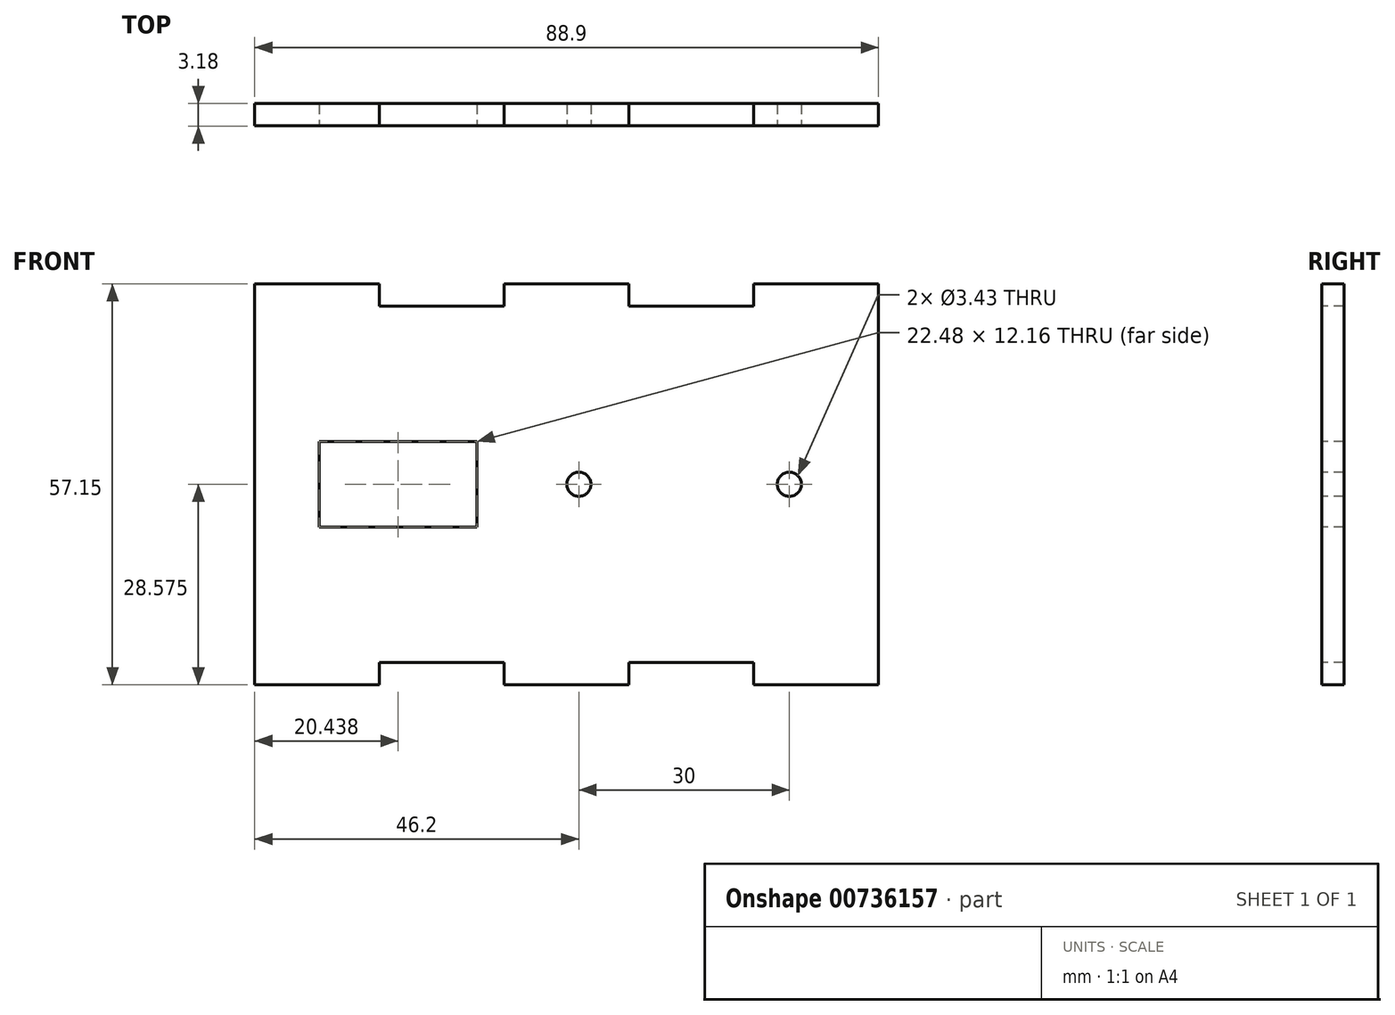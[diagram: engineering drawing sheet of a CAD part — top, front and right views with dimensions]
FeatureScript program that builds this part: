
annotation { "Feature Type Name" : "Feature", "Feature Type Description" : "" }
export const myFeature = defineFeature(function(context is Context, id is Id, definition is map)
    precondition{}
    {
        {
            var Q0;
            Q0=qCreatedBy(makeId("Top.planeOp"),FACE);
            var sketch = newSketch(context, id + "F0", { "sketchPlane" : qUnion([Q0])});
            skLineSegment(sketch, "E0.bottom", {"start": v(44.45, 9.52) * mm, "end": v(-44.45, 9.52) * mm});
            skLineSegment(sketch, "E0.top", {"start": v(44.45, -9.53) * mm, "end": v(-44.45, -9.53) * mm});
            skLineSegment(sketch, "E0.left", {"start": v(44.45, 9.52) * mm, "end": v(44.45, -9.53) * mm});
            skLineSegment(sketch, "E0.right", {"start": v(-44.45, 9.52) * mm, "end": v(-44.45, -9.53) * mm});
            skPoint(sketch, "E0.middle", {"position": v(0, 0) * mm});
            skLineSegment(sketch, "E1", {"start": v(-44.45, 6.35) * mm, "end": v(44.45, 6.35) * mm});
            skLineSegment(sketch, "E2", {"start": v(-44.45, -6.35) * mm, "end": v(44.45, -6.35) * mm});
            skSolve(sketch);
        }
        {
            var Q0;
            {var subQ0=sQuery(id+"F0.wireOp",EDGE,"E0.bottom");Q0=makeQuery(id+"F0.imprint","IMPRINT",FACE,{"disambiguationData":[TD([[makeQuery(id+"F0.imprint","IMPRINT",EDGE,{"derivedFrom":subQ0}),1.0]])]});}
            var Q1;
            {var subQ0=sQuery(id+"F0.wireOp",EDGE,"E0.top");Q1=makeQuery(id+"F0.imprint","IMPRINT",FACE,{"disambiguationData":[TD([[makeQuery(id+"F0.imprint","IMPRINT",EDGE,{"derivedFrom":subQ0}),-1.0]])]});}
            extrude(context, id + "F1", {"entities" : qUnion([Q0, Q1]), "depth" : 57.15 * mm, "offsetDistance" : 25.4 * mm});
        }
        {
            var Q0;
            Q0=makeQuery(id+"F1.opExtrude","SWEPT_FACE",FACE,{"disambiguationData":[OSD([sQuery(id+"F0.wireOp",EDGE,"E0.top")])]});
            var sketch = newSketch(context, id + "F2", { "sketchPlane" : qUnion([Q0])});
            skLineSegment(sketch, "E3", {"start": v(-44.45, 3.18) * mm, "end": v(44.45, 3.18) * mm});
            skLineSegment(sketch, "E4", {"start": v(-44.45, 53.98) * mm, "end": v(44.45, 53.98) * mm});
            skCircle(sketch, "E5", {"center": v(31.75, 28.58) * mm, "radius": 1.71 * mm});
            skPoint(sketch, "E5.centerSnap0", {"position": v(44.45, 28.58) * mm});
            skCircle(sketch, "E6", {"center": v(1.75, 28.58) * mm, "radius": 1.71 * mm});
            skLineSegment(sketch, "E7.bottom", {"start": v(-12.77, 34.66) * mm, "end": v(-35.25, 34.66) * mm});
            skLineSegment(sketch, "E7.top", {"start": v(-12.77, 22.5) * mm, "end": v(-35.25, 22.5) * mm});
            skLineSegment(sketch, "E7.left", {"start": v(-12.77, 34.66) * mm, "end": v(-12.77, 22.5) * mm});
            skLineSegment(sketch, "E7.right", {"start": v(-35.25, 34.66) * mm, "end": v(-35.25, 22.5) * mm});
            skPoint(sketch, "E7.middle", {"position": v(-24.01, 28.58) * mm});
            skLineSegment(sketch, "E8", {"start": v(-26.67, 57.15) * mm, "end": v(-26.67, 53.98) * mm});
            skLineSegment(sketch, "E9", {"start": v(-8.9, 57.15) * mm, "end": v(-8.9, 53.98) * mm});
            skLineSegment(sketch, "E10", {"start": v(8.89, 57.15) * mm, "end": v(8.89, 53.98) * mm});
            skPoint(sketch, "E10.endSnap0", {"position": v(0, 53.98) * mm});
            skLineSegment(sketch, "E11", {"start": v(26.67, 57.15) * mm, "end": v(26.67, 53.98) * mm});
            skLineSegment(sketch, "E12", {"start": v(-44.45, 28.58) * mm, "end": v(44.45, 28.58) * mm});
            skLineSegment(sketch, "E13.MirrorCS", {"start": v(26.67, 0) * mm, "end": v(26.67, 3.18) * mm});
            skLineSegment(sketch, "E14.MirrorCS", {"start": v(8.9, 0) * mm, "end": v(8.9, 3.18) * mm});
            skLineSegment(sketch, "E15.MirrorCS", {"start": v(-8.89, 0) * mm, "end": v(-8.89, 3.18) * mm});
            skLineSegment(sketch, "E16.MirrorCS", {"start": v(-26.67, 0) * mm, "end": v(-26.67, 3.18) * mm});
            skSolve(sketch);
        }
        {
            var Q0;
            {var subQ0=sQuery(id+"F2.wireOp",EDGE,"E8");Q0=makeQuery(id+"F2.imprint","IMPRINT",FACE,{"disambiguationData":[TD([[makeQuery(id+"F2.imprint","IMPRINT",EDGE,{"derivedFrom":subQ0}),1.0]])]});}
            var Q1;
            {var subQ0=sQuery(id+"F2.wireOp",EDGE,"E10");Q1=makeQuery(id+"F2.imprint","IMPRINT",FACE,{"disambiguationData":[TD([[makeQuery(id+"F2.imprint","IMPRINT",EDGE,{"derivedFrom":subQ0}),1.0]])]});}
            var Q2;
            {var subQ0=sQuery(id+"F2.wireOp",EDGE,"E15.MirrorCS");Q2=makeQuery(id+"F2.imprint","IMPRINT",FACE,{"disambiguationData":[TD([[makeQuery(id+"F2.imprint","IMPRINT",EDGE,{"derivedFrom":subQ0}),1.0]])]});}
            var Q3;
            {var subQ0=sQuery(id+"F2.wireOp",EDGE,"E13.MirrorCS");Q3=makeQuery(id+"F2.imprint","IMPRINT",FACE,{"disambiguationData":[TD([[makeQuery(id+"F2.imprint","IMPRINT",EDGE,{"derivedFrom":subQ0}),1.0]])]});}
            var Q4;
            {var subQ0=sQuery(id+"F2.wireOp",EDGE,"E7.bottom");Q4=makeQuery(id+"F2.imprint","IMPRINT",FACE,{"disambiguationData":[TD([[makeQuery(id+"F2.imprint","IMPRINT",EDGE,{"derivedFrom":subQ0}),1.0]])]});}
            var Q5;
            {var subQ0=sQuery(id+"F2.wireOp",EDGE,"E7.top");Q5=makeQuery(id+"F2.imprint","IMPRINT",FACE,{"disambiguationData":[TD([[makeQuery(id+"F2.imprint","IMPRINT",EDGE,{"derivedFrom":subQ0}),-1.0]])]});}
            var Q6;
            {var subQ0=sQuery(id+"F2.wireOp",EDGE,"E12");var subQ1=sQuery(id+"F2.wireOp",EDGE,"E6");var subQ2=makeQuery(id+"F2.imprint","INTERSECT",VERTEX,{"disambiguationData":[OD(0.0)],"derivedFrom":[subQ1,subQ0]});Q6=makeQuery(id+"F2.imprint","IMPRINT",FACE,{"disambiguationData":[TD([[makeQuery(id+"F2.imprint","IMPRINT",EDGE,{"disambiguationData":[TD([[subQ2,1.0]])],"derivedFrom":subQ1}),1.0]])]});}
            var Q7;
            {var subQ0=sQuery(id+"F2.wireOp",EDGE,"E12");var subQ1=sQuery(id+"F2.wireOp",EDGE,"E6");var subQ2=makeQuery(id+"F2.imprint","INTERSECT",VERTEX,{"disambiguationData":[OD(0.0)],"derivedFrom":[subQ1,subQ0]});Q7=makeQuery(id+"F2.imprint","IMPRINT",FACE,{"disambiguationData":[TD([[makeQuery(id+"F2.imprint","IMPRINT",EDGE,{"disambiguationData":[TD([[subQ2,-1.0]])],"derivedFrom":subQ1}),1.0]])]});}
            var Q8;
            {var subQ0=sQuery(id+"F2.wireOp",EDGE,"E12");var subQ1=sQuery(id+"F2.wireOp",EDGE,"E5");var subQ2=makeQuery(id+"F2.imprint","INTERSECT",VERTEX,{"disambiguationData":[OD(0.0)],"derivedFrom":[subQ1,subQ0]});Q8=makeQuery(id+"F2.imprint","IMPRINT",FACE,{"disambiguationData":[TD([[makeQuery(id+"F2.imprint","IMPRINT",EDGE,{"disambiguationData":[TD([[subQ2,1.0]])],"derivedFrom":subQ1}),1.0]])]});}
            var Q9;
            {var subQ0=sQuery(id+"F2.wireOp",EDGE,"E12");var subQ1=sQuery(id+"F2.wireOp",EDGE,"E5");var subQ2=makeQuery(id+"F2.imprint","INTERSECT",VERTEX,{"disambiguationData":[OD(0.0)],"derivedFrom":[subQ1,subQ0]});Q9=makeQuery(id+"F2.imprint","IMPRINT",FACE,{"disambiguationData":[TD([[makeQuery(id+"F2.imprint","IMPRINT",EDGE,{"disambiguationData":[TD([[subQ2,-1.0]])],"derivedFrom":subQ1}),1.0]])]});}
            var Q10;
            Q10=makeQuery(id+"F1.opExtrude","SWEPT_FACE",FACE,{"disambiguationData":[OSD([sQuery(id+"F0.wireOp",EDGE,"E2")])]});
            var Q11;
            Q11=makeQuery(id+"F1.opExtrude","SWEPT_FACE",FACE,{"disambiguationData":[OSD([sQuery(id+"F0.wireOp",EDGE,"E0.top")])]});
            extrude(context, id + "F3", {"entities" : qUnion([Q0, Q1, Q2, Q3, Q4, Q5, Q6, Q7, Q8, Q9, Q10]), "operationType" : NewBodyOperationType.REMOVE, "endBound" : BoundingType.THROUGH_ALL, "oppositeDirection" : true, "depth" : 25.4 * mm, "endBoundEntityFace" : qUnion([Q11]), "offsetDistance" : 25.4 * mm});
        }
    });
